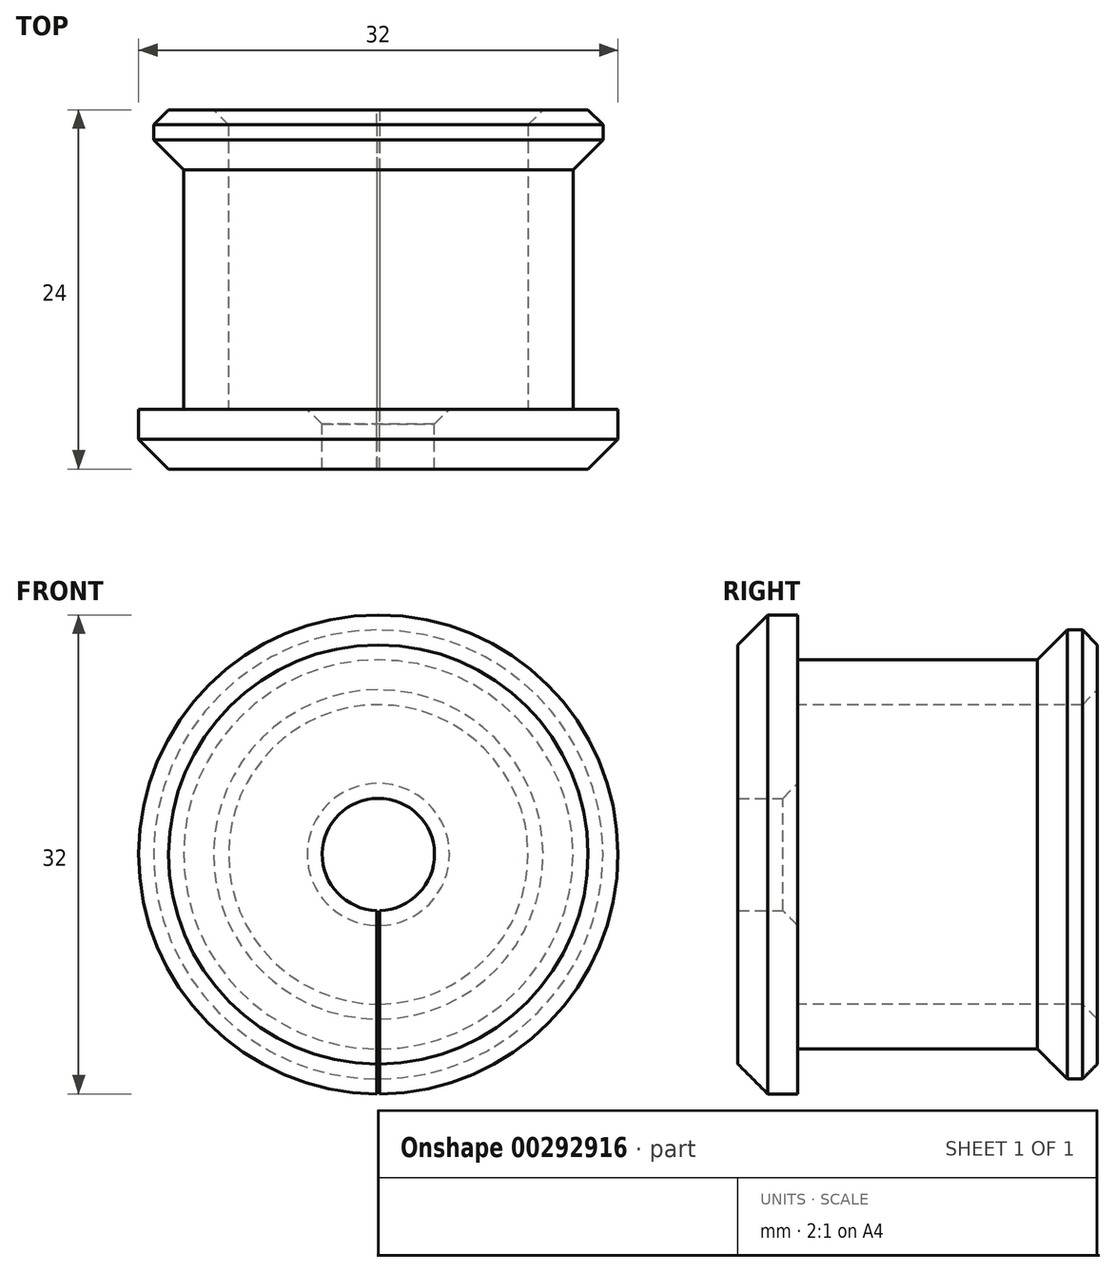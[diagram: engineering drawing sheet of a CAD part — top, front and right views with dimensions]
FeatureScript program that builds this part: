
annotation { "Feature Type Name" : "Feature", "Feature Type Description" : "" }
export const myFeature = defineFeature(function(context is Context, id is Id, definition is map)
    precondition{}
    {
        {
            var Q0;
            Q0=qCreatedBy(makeId("Front.planeOp"),FACE);
            var sketch = newSketch(context, id + "F0", { "sketchPlane" : qUnion([Q0])});
            skCircle(sketch, "E0", {"center": v(0, 0) * mm, "radius": 13 * mm});
            skCircle(sketch, "E1", {"center": v(0, 0) * mm, "radius": 16 * mm});
            skCircle(sketch, "E2", {"center": v(0, 0) * mm, "radius": 3.75 * mm});
            skCircle(sketch, "E3", {"center": v(0, 0) * mm, "radius": 15 * mm});
            skCircle(sketch, "E4", {"center": v(0, 0) * mm, "radius": 10 * mm});
            skSolve(sketch);
        }
        {
            var Q0;
            Q0=makeQuery(id+"F0.imprint","IMPRINT",FACE,{"disambiguationData":[TD([[makeQuery(id+"F0.imprint","IMPRINT",EDGE,{"derivedFrom":sQuery(id+"F0.wireOp",EDGE,"E1")}),1.0]])]});
            var Q1;
            Q1=makeQuery(id+"F0.imprint","IMPRINT",FACE,{"disambiguationData":[TD([[makeQuery(id+"F0.imprint","IMPRINT",EDGE,{"derivedFrom":sQuery(id+"F0.wireOp",EDGE,"E0")}),-1.0]])]});
            var Q2;
            Q2=makeQuery(id+"F0.imprint","IMPRINT",FACE,{"disambiguationData":[TD([[makeQuery(id+"F0.imprint","IMPRINT",EDGE,{"derivedFrom":sQuery(id+"F0.wireOp",EDGE,"E0")}),1.0]])]});
            var Q3;
            Q3=makeQuery(id+"F0.imprint","IMPRINT",FACE,{"disambiguationData":[TD([[makeQuery(id+"F0.imprint","IMPRINT",EDGE,{"derivedFrom":sQuery(id+"F0.wireOp",EDGE,"E2")}),-1.0]])]});
            extrude(context, id + "F1", {"entities" : qUnion([Q0, Q1, Q2, Q3]), "depth" : 4 * mm});
        }
        {
            var Q0;
            Q0=makeQuery(id+"F0.imprint","IMPRINT",FACE,{"disambiguationData":[TD([[makeQuery(id+"F0.imprint","IMPRINT",EDGE,{"derivedFrom":sQuery(id+"F0.wireOp",EDGE,"E0")}),1.0]])]});
            extrude(context, id + "F2", {"entities" : qUnion([Q0]), "operationType" : NewBodyOperationType.ADD, "oppositeDirection" : true, "depth" : 16 * mm});
        }
        {
            var Q0;
            Q0=makeQuery(id+"F2.opExtrude","CAP_FACE",FACE,{"disambiguationData":[OSD([sQuery(id+"F0.wireOp",EDGE,"E0"),sQuery(id+"F0.wireOp",EDGE,"E4")])],"isStart":false});
            cPlane(context, id + "F3", {"entities" : qUnion([Q0]), "cplaneType" : CPlaneType.OFFSET, "offset" : 0 * mm, "width" : 150 * mm, "height" : 150 * mm});
        }
        {
            var Q0;
            Q0=qCreatedBy(id+"F3.planeOp",FACE);
            var sketch = newSketch(context, id + "F4", { "sketchPlane" : qUnion([Q0])});
            skCircle(sketch, "E5", {"center": v(0, 0) * mm, "radius": 15 * mm});
            skCircle(sketch, "E6", {"center": v(0, 0) * mm, "radius": 10 * mm});
            skSolve(sketch);
        }
        {
            var Q0;
            Q0=makeQuery(id+"F4.imprint","IMPRINT",FACE,{"disambiguationData":[TD([[makeQuery(id+"F4.imprint","IMPRINT",EDGE,{"derivedFrom":sQuery(id+"F4.wireOp",EDGE,"E5")}),1.0]])]});
            extrude(context, id + "F5", {"entities" : qUnion([Q0]), "operationType" : NewBodyOperationType.ADD, "depth" : 4 * mm});
        }
        {
            var Q0;
            Q0=makeQuery(id+"F1.opExtrude","CAP_EDGE",EDGE,{"disambiguationData":[OSD([sQuery(id+"F0.wireOp",EDGE,"E1")])],"isStart":false});
            chamfer(context, id + "F6", {"entities" : qUnion([Q0]), "width" : 2 * mm, "tangentPropagation" : true});
        }
        {
            var Q0;
            Q0=makeQuery(id+"F5.opExtrude","CAP_EDGE",EDGE,{"disambiguationData":[OSD([sQuery(id+"F4.wireOp",EDGE,"E6")])],"isStart":false});
            var Q1;
            Q1=makeQuery(id+"F1.opExtrude","CAP_EDGE",EDGE,{"disambiguationData":[OSD([sQuery(id+"F0.wireOp",EDGE,"E2")])],"isStart":true});
            var Q2;
            Q2=makeQuery(id+"F5.opExtrude","CAP_EDGE",EDGE,{"disambiguationData":[OSD([sQuery(id+"F4.wireOp",EDGE,"E5")])],"isStart":false});
            chamfer(context, id + "F7", {"entities" : qUnion([Q0, Q1, Q2]), "width" : 1 * mm, "tangentPropagation" : true});
        }
        {
            var Q0;
            Q0=makeQuery(id+"F5.opExtrude","CAP_EDGE",EDGE,{"disambiguationData":[OSD([sQuery(id+"F4.wireOp",EDGE,"E5")])],"isStart":true});
            chamfer(context, id + "F8", {"entities" : qUnion([Q0]), "width" : 2 * mm, "tangentPropagation" : true});
        }
        {
            var Q0;
            Q0=qCreatedBy(makeId("Front.planeOp"),FACE);
            var sketch = newSketch(context, id + "F9", { "sketchPlane" : qUnion([Q0])});
            skLineSegment(sketch, "E7", {"start": v(-0.1, 0) * mm, "end": v(0.1, 0) * mm});
            skLineSegment(sketch, "E8", {"start": v(0.1, 0) * mm, "end": v(0.1, -20) * mm});
            skLineSegment(sketch, "E9", {"start": v(0.1, -20) * mm, "end": v(-0.1, -20) * mm});
            skLineSegment(sketch, "E10", {"start": v(-0.1, -20) * mm, "end": v(-0.1, 0) * mm});
            skSolve(sketch);
        }
        {
            var Q0;
            Q0 = qSketchRegion(id + "F9", true);
            extrude(context, id + "F10", {"entities" : qUnion([Q0]), "operationType" : NewBodyOperationType.REMOVE, "endBound" : BoundingType.SYMMETRIC, "oppositeDirection" : true, "depth" : 50 * mm});
        }
    });
